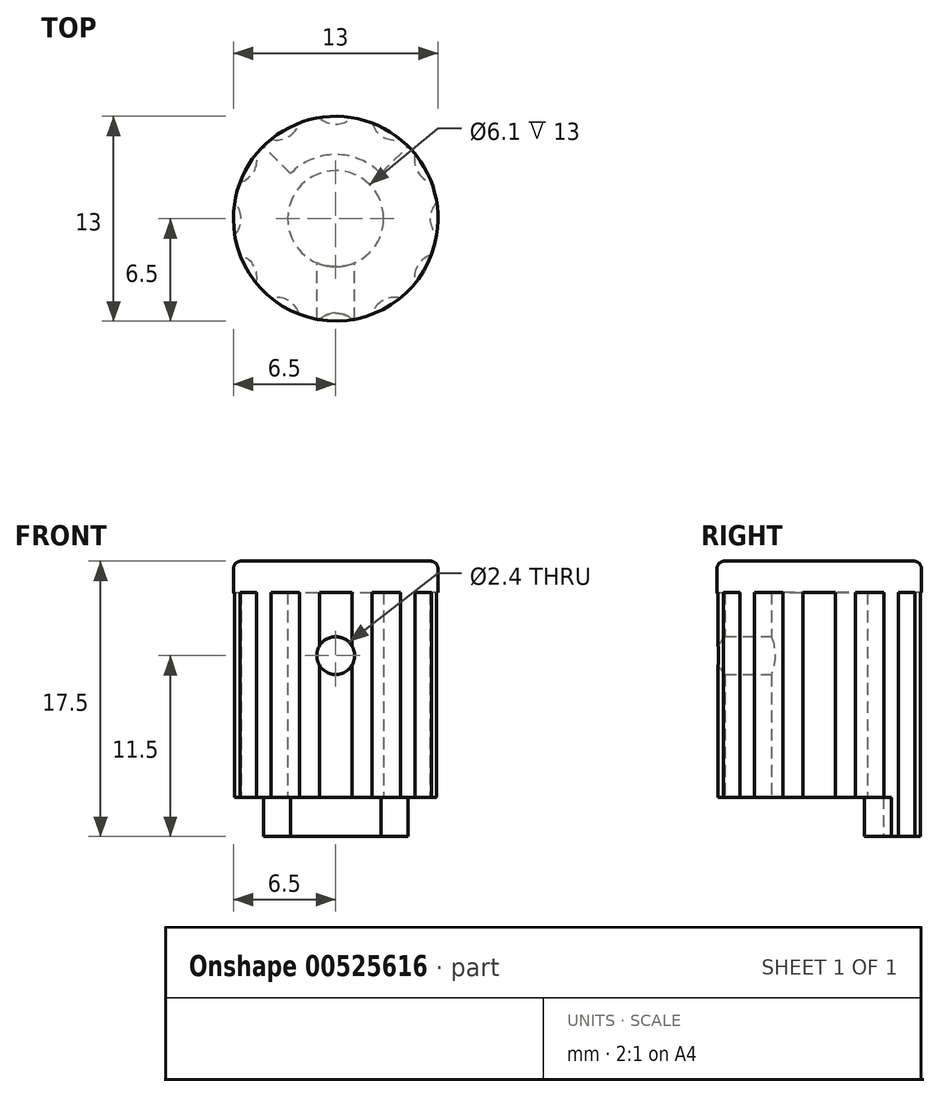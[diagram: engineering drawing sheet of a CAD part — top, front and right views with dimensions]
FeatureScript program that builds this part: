
annotation { "Feature Type Name" : "Feature", "Feature Type Description" : "" }
export const myFeature = defineFeature(function(context is Context, id is Id, definition is map)
    precondition{}
    {
        {
            var Q0;
            Q0=qCreatedBy(makeId("Front.planeOp"),FACE);
            var sketch = newSketch(context, id + "F0", { "sketchPlane" : qUnion([Q0])});
            skLineSegment(sketch, "E0", {"start": v(0, -2.23) * mm, "end": v(0, -5.1) * mm, "construction": true});
            skLineSegment(sketch, "E1", {"start": v(0, 0) * mm, "end": v(-5, 0) * mm});
            skLineSegment(sketch, "E2", {"start": v(-5, 0) * mm, "end": v(-5, 0) * mm});
            skLineSegment(sketch, "E3", {"start": v(-5, 0) * mm, "end": v(-6.5, 0) * mm});
            skLineSegment(sketch, "E4", {"start": v(-6.5, 0) * mm, "end": v(-6.5, 15) * mm});
            skLineSegment(sketch, "E5", {"start": v(-6.5, 15) * mm, "end": v(0, 15) * mm});
            skLineSegment(sketch, "E6", {"start": v(0, 0) * mm, "end": v(0, 15) * mm});
            skSolve(sketch);
        }
        {
            var Q0;
            Q0=qSketchRegion(id+"F0",true);
            var Q1;
            Q1=sQuery(id+"F0.wireOp",EDGE,"E0");
            revolve(context, id + "F1", {"entities" : qUnion([Q0]), "axis" : qUnion([Q1]), "revolveType" : RevolveType.FULL});
        }
        {
            var Q0;
            Q0=makeQuery(id+"F1.opRevolve","SWEPT_FACE",FACE,{"disambiguationData":[OSD([sQuery(id+"F0.wireOp",EDGE,"E1")])]});
            var sketch = newSketch(context, id + "F2", { "sketchPlane" : qUnion([Q0])});
            skCircle(sketch, "E7", {"center": v(0, 0) * mm, "radius": 3.05 * mm});
            skSolve(sketch);
        }
        {
            var Q0;
            Q0=qSketchRegion(id+"F2",true);
            extrude(context, id + "F3", {"entities" : qUnion([Q0]), "operationType" : NewBodyOperationType.REMOVE, "oppositeDirection" : true, "depth" : 13 * mm, "offsetDistance" : 25 * mm});
        }
        {
            var Q0;
            Q0=makeQuery(id+"F1.opRevolve","SWEPT_EDGE",EDGE,{"disambiguationData":[OSD([sQuery(id+"F0.wireOp",EDGE,"E4"),sQuery(id+"F0.wireOp",EDGE,"E5")])]});
            fillet(context, id + "F4", {"entities" : qUnion([Q0]), "radius" : 0.5 * mm, "tangentPropagation" : true, "allowEdgeOverflow" : false});
        }
        {
            var Q0;
            Q0=qCreatedBy(makeId("Front.planeOp"),FACE);
            var sketch = newSketch(context, id + "F5", { "sketchPlane" : qUnion([Q0])});
            skCircle(sketch, "E8", {"center": v(0, 9) * mm, "radius": 1.2 * mm});
            skSolve(sketch);
        }
        {
            var Q0;
            Q0=qSketchRegion(id+"F5",true);
            extrude(context, id + "F6", {"entities" : qUnion([Q0]), "operationType" : NewBodyOperationType.REMOVE, "depth" : 7 * mm, "offsetDistance" : 25 * mm});
        }
        {
            var Q0;
            Q0=makeQuery(id+"F1.opRevolve","SWEPT_FACE",FACE,{"disambiguationData":[OSD([sQuery(id+"F0.wireOp",EDGE,"E1"),sQuery(id+"F0.wireOp",EDGE,"E3")])]});
            var sketch = newSketch(context, id + "F7", { "sketchPlane" : qUnion([Q0])});
            skCircle(sketch, "E9", {"center": v(-7.5, 0) * mm, "radius": 1.5 * mm});
            skCircle(sketch, "E10.1.0", {"center": v(-6.5, -3.75) * mm, "radius": 1.5 * mm});
            skCircle(sketch, "E10.2.0", {"center": v(-3.75, -6.5) * mm, "radius": 1.5 * mm});
            skCircle(sketch, "E10.3.0", {"center": v(0, -7.5) * mm, "radius": 1.5 * mm});
            skCircle(sketch, "E10.4.0", {"center": v(3.75, -6.5) * mm, "radius": 1.5 * mm});
            skCircle(sketch, "E10.5.0", {"center": v(6.5, -3.75) * mm, "radius": 1.5 * mm});
            skCircle(sketch, "E10.6.0", {"center": v(7.5, 0) * mm, "radius": 1.5 * mm});
            skCircle(sketch, "E10.7.0", {"center": v(6.5, 3.75) * mm, "radius": 1.5 * mm});
            skCircle(sketch, "E10.8.0", {"center": v(3.75, 6.5) * mm, "radius": 1.5 * mm});
            skCircle(sketch, "E10.9.0", {"center": v(0, 7.5) * mm, "radius": 1.5 * mm});
            skCircle(sketch, "E10.10.0", {"center": v(-3.75, 6.5) * mm, "radius": 1.5 * mm});
            skCircle(sketch, "E10.11.0", {"center": v(-6.5, 3.75) * mm, "radius": 1.5 * mm});
            skPoint(sketch, "E10.center", {"position": v(0, 0) * mm});
            skSolve(sketch);
        }
        {
            var Q0;
            Q0=qSketchRegion(id+"F7",true);
            extrude(context, id + "F8", {"entities" : qUnion([Q0]), "operationType" : NewBodyOperationType.REMOVE, "oppositeDirection" : true, "depth" : 13 * mm, "offsetDistance" : 25 * mm});
        }
        {
            var Q0;
            Q0=makeQuery(id+"F1.opRevolve","SWEPT_FACE",FACE,{"disambiguationData":[OSD([sQuery(id+"F0.wireOp",EDGE,"E1"),sQuery(id+"F0.wireOp",EDGE,"E3")])]});
            var sketch = newSketch(context, id + "F9", { "sketchPlane" : qUnion([Q0])});
            skLineSegment(sketch, "E11", {"start": v(0, 0) * mm, "end": v(0, 1.36) * mm, "construction": true});
            skLineSegment(sketch, "E12", {"start": v(0, 0) * mm, "end": v(-5.66, -5.66) * mm});
            skArc(sketch, "E13", {"start": v(5.66, -5.66) * mm, "mid": v(0, 8) * mm, "end": v(-5.66, -5.66) * mm});
            skLineSegment(sketch, "E14", {"start": v(0, 0) * mm, "end": v(5.66, -5.66) * mm});
            skArc(sketch, "E15", {"start": v(-5.66, -5.66) * mm, "mid": v(0, -8.89) * mm, "end": v(5.66, -5.66) * mm, "construction": true});
            skLineSegment(sketch, "E16", {"start": v(0, 0) * mm, "end": v(11.71, 0) * mm, "construction": true});
            skSolve(sketch);
        }
        {
            var Q0;
            Q0 = qSketchRegion(id + "F9", true);
            extrude(context, id + "F10", {"entities" : qUnion([Q0]), "operationType" : NewBodyOperationType.REMOVE, "oppositeDirection" : true, "depth" : 2.5 * mm, "offsetDistance" : 25 * mm});
        }
        {
            var Q0;
            Q0=makeQuery(id+"F10.boolean.opBoolean","COPY",FACE,{"derivedFrom":makeQuery(id+"F10.opExtrude","CAP_FACE",FACE,{"disambiguationData":[OSD([sQuery(id+"F9.wireOp",EDGE,"E12"),sQuery(id+"F9.wireOp",EDGE,"E13"),sQuery(id+"F9.wireOp",EDGE,"E14")])],"isStart":false})});
            var Q1;
            Q1=makeQuery(id+"F1.opRevolve","SWEPT_FACE",FACE,{"disambiguationData":[OSD([sQuery(id+"F0.wireOp",EDGE,"E1"),sQuery(id+"F0.wireOp",EDGE,"E3")])]});
            extrude(context, id + "F11", {"entities" : qUnion([Q0, Q1]), "operationType" : NewBodyOperationType.ADD, "depth" : 2.5 * mm, "offsetDistance" : 25 * mm});
        }
        {
            var Q0;
            Q0=makeQuery(id+"F11.opExtrude","CAP_FACE",FACE,{"disambiguationData":[OSD([sQuery(id+"F0.wireOp",EDGE,"E1"),sQuery(id+"F0.wireOp",EDGE,"E3")])],"isStart":false});
            var sketch = newSketch(context, id + "F12", { "sketchPlane" : qUnion([Q0])});
            skArc(sketch, "E17.0", {"start": v(-2.16, -2.16) * mm, "mid": v(0, -3.05) * mm, "end": v(2.16, -2.16) * mm});
            skLineSegment(sketch, "E18", {"start": v(2.16, -2.16) * mm, "end": v(2.86, -2.86) * mm});
            skLineSegment(sketch, "E19", {"start": v(-2.16, -2.16) * mm, "end": v(-2.86, -2.86) * mm});
            skArc(sketch, "E20", {"start": v(-2.86, -2.86) * mm, "mid": v(0, -4.07) * mm, "end": v(2.86, -2.86) * mm});
            skSolve(sketch);
        }
        {
            var Q0;
            Q0 = qSketchRegion(id + "F12", true);
            extrude(context, id + "F13", {"entities" : qUnion([Q0]), "operationType" : NewBodyOperationType.REMOVE, "oppositeDirection" : true, "depth" : 2.5 * mm, "offsetDistance" : 25 * mm});
        }
    });
